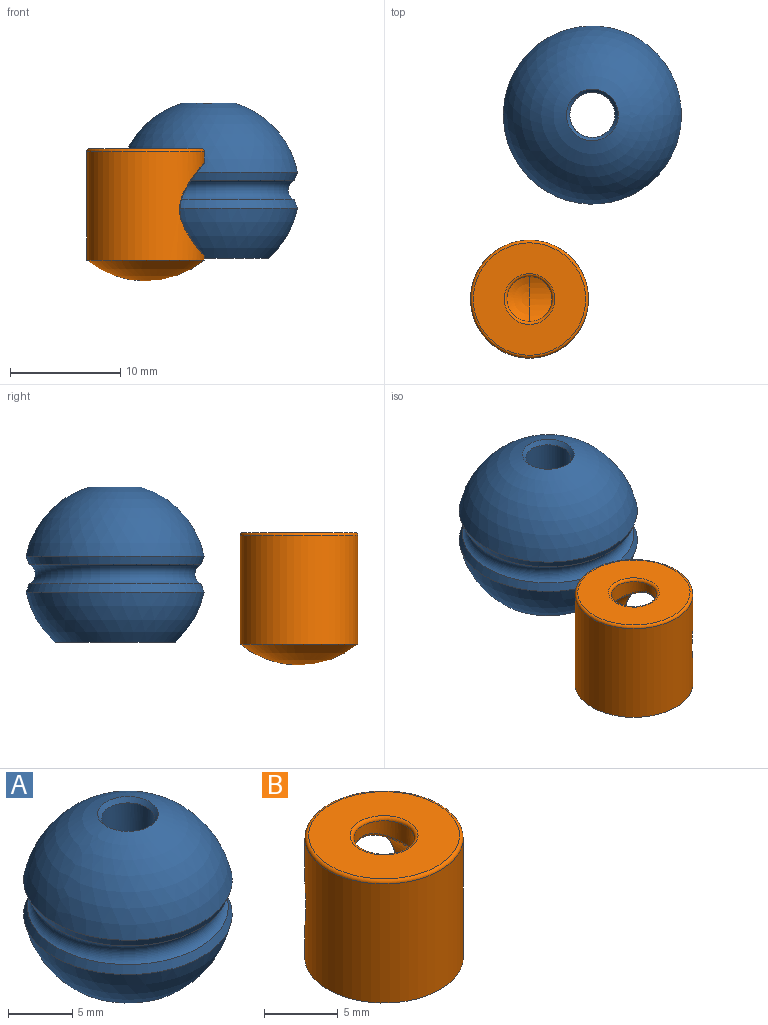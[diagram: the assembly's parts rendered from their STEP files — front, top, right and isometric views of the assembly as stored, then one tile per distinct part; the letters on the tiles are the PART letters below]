
ASSEMBLY  parts=2 mates=1
PART A: 16 faces, bbox 17.9x17.9x14.1 mm
  f0: cylinder r=2.05mm len=4.1mm, axis (0,0,-1), area 45.2mm2, adj f1,f14
  f1: cone r=2.35mm half-angle=36.9deg, axis (0,0,1), area 6.9mm2, adj f0,f2
  f2: sphere r=8.25mm, area 325.4mm2, adj f1,f3
  f3: cone r=7.79mm half-angle=21.9deg, axis (0,0,1), area 39.9mm2, adj f2,f4
  f4: torus R=8.25mm, axis (0,0,-1), area 102.1mm2, adj f3,f5
  f5: cone r=7.79mm half-angle=21.9deg, axis (0,0,-1), area 39.9mm2, adj f4,f6
  f6: sphere r=8.25mm, area 236.6mm2, adj f5,f7
  f7: cylinder r=5.45mm len=10.9mm, axis (0,0,-1), area 62.5mm2, adj f6,f8
  f8: torus R=6.45mm, axis (0,0,-1), area 11.7mm2, adj f7,f9
  f9: revolved ~12.3x12.3mm, area 352mm2, adj f8,f10
  f10: torus R=3.74mm, axis (0,0,-1), area 38.3mm2, adj f9,f11
  f11: torus R=3.45mm, axis (0,0,-1), area 7mm2, adj f10,f12
  f12: cylinder r=3.15mm len=6.3mm, axis (0,0,-1), area 29.9mm2, adj f11,f15
  f13: plane 5.8x5.8mm, normal (0,0,-1), area 9.8mm2, adj f14,f15
  f14: torus R=2.3mm, axis (0,0,1), area 5.3mm2, adj f0,f13
  f15: torus R=2.9mm, axis (0,0,1), area 7.5mm2, adj f12,f13
PART B: 11 faces, bbox 11.6x11.6x12 mm
  f0: sphere r=8.5mm, area 101.2mm2, adj f3
  f1: sphere r=4.15mm, area 100.2mm2, adj f4,f7
  f2: cylinder r=2.05mm len=4.1mm, axis (0,0,-1), area 17.3mm2, adj f7,f8,f9
  f3: cylinder r=5.35mm len=10.7mm, axis (0,0,-1), area 265.6mm2, adj f0,f5,f10
  f4: cylinder r=4.15mm len=8.3mm, axis (0,-1,0), area 101.1mm2, adj f1,f5,f8
  f5: bspline ~8.76x8.56mm, area 7.1mm2, adj f3,f4
  f6: plane 10.2x10.2mm, normal (0,0,1), area 65.1mm2, adj f9,f10
  f7: torus R=2.3mm, axis (0,0,-1), area 1.7mm2, adj f1,f2,f8
  f8: bspline ~4.34x2.76mm, area 2.2mm2, adj f2,f4,f7
  f9: torus R=2.3mm, axis (0,0,-1), area 5.3mm2, adj f2,f6
  f10: torus R=5.1mm, axis (0,0,-1), area 13mm2, adj f3,f6
PLACE A rot(axis=(0,0,-1),180deg) t=(0,0,-4)mm
PLACE B rot(axis=(0,0,-1),90deg) t=(-5.71,-16.71,-3.75)mm
MATE planar B.f2 <-> A.f0  axis (0,0,1) through (-5.71,-16.71,-0.25)mm
